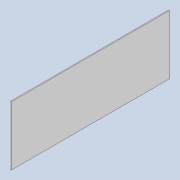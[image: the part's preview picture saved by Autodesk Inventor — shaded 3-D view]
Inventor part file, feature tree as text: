
AUTODESK INVENTOR PART (.ipt)
format: ipt  version: 2020 (Build 240168000, 168)  size: 75,264 bytes
history: native  units: mm
features: extrude x1, sketch x1
ambient origin geometry x8: Origin, YZ Plane, XZ Plane, XY Plane, X Axis, Y Axis, Z Axis, Center Point
bodies: Solid1 (feature_tree)
feature tree (2):
  extrude  "Extrusion1"  Depth=0.05mm
  sketch  "Sketch1"  dims[d0=8.0mm d1=0.05mm d2=3.0mm d3=0.0mm]
